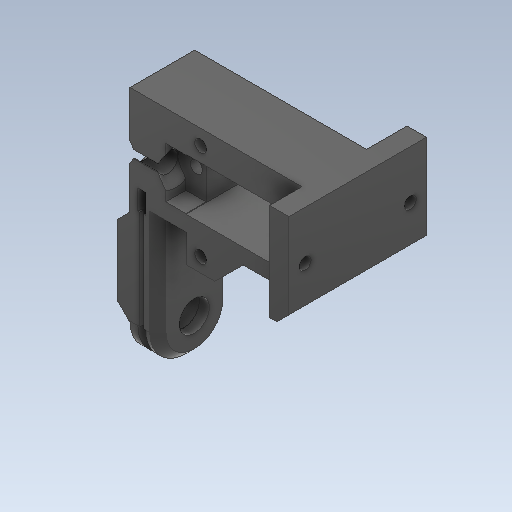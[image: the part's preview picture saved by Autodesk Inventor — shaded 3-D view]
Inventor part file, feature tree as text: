
AUTODESK INVENTOR PART (.ipt)
format: ipt  version: 2020 (Build 240168000, 168)  size: 470,528 bytes
history: native  units: in
note: dims shown in document units (in); Inventor stores cm internally (conversion verified against a paired STEP export)
features: sketch x38, other x3, plane x1
ambient origin geometry x8: Origin, YZ Plane, XZ Plane, XY Plane, X Axis, Y Axis, Z Axis, Center Point
bodies: Solid1 (feature_tree)
feature tree (42):
  other  "FermurSupport.ipt"
  other  "Solid1::FermurSupport.ipt"
  other  "TaggingFeature1"
  sketch  "Sketch1"  dims[d0=0.3937in]
  sketch  "Sketch2"
  sketch  "Sketch3"
  sketch  "Sketch4"
  sketch  "Sketch5"
  sketch  "Sketch6"
  sketch  "Sketch8"
  sketch  "Sketch10"
  sketch  "Sketch11"
  sketch  "Sketch12"
  sketch  "Sketch13"
  sketch  "Sketch14"
  sketch  "Sketch15"
  sketch  "Sketch17"
  sketch  "Sketch19"
  sketch  "Sketch21"
  sketch  "Sketch22"
  sketch  "Sketch23"
  sketch  "Sketch26"
  sketch  "Sketch27"
  sketch  "Sketch29"
  sketch  "Sketch32"
  sketch  "Sketch33"
  sketch  "Sketch36"
  sketch  "Sketch37"
  sketch  "Sketch38"
  sketch  "Sketch39"
  sketch  "Sketch41"
  sketch  "Sketch42"
  sketch  "Sketch43"
  sketch  "Sketch44"
  sketch  "Sketch45"
  sketch  "Sketch46"
  sketch  "Sketch47"
  sketch  "Sketch48"
  sketch  "Sketch49"
  sketch  "Sketch50"
  sketch  "Sketch51"
  plane  "Work Plane1"
